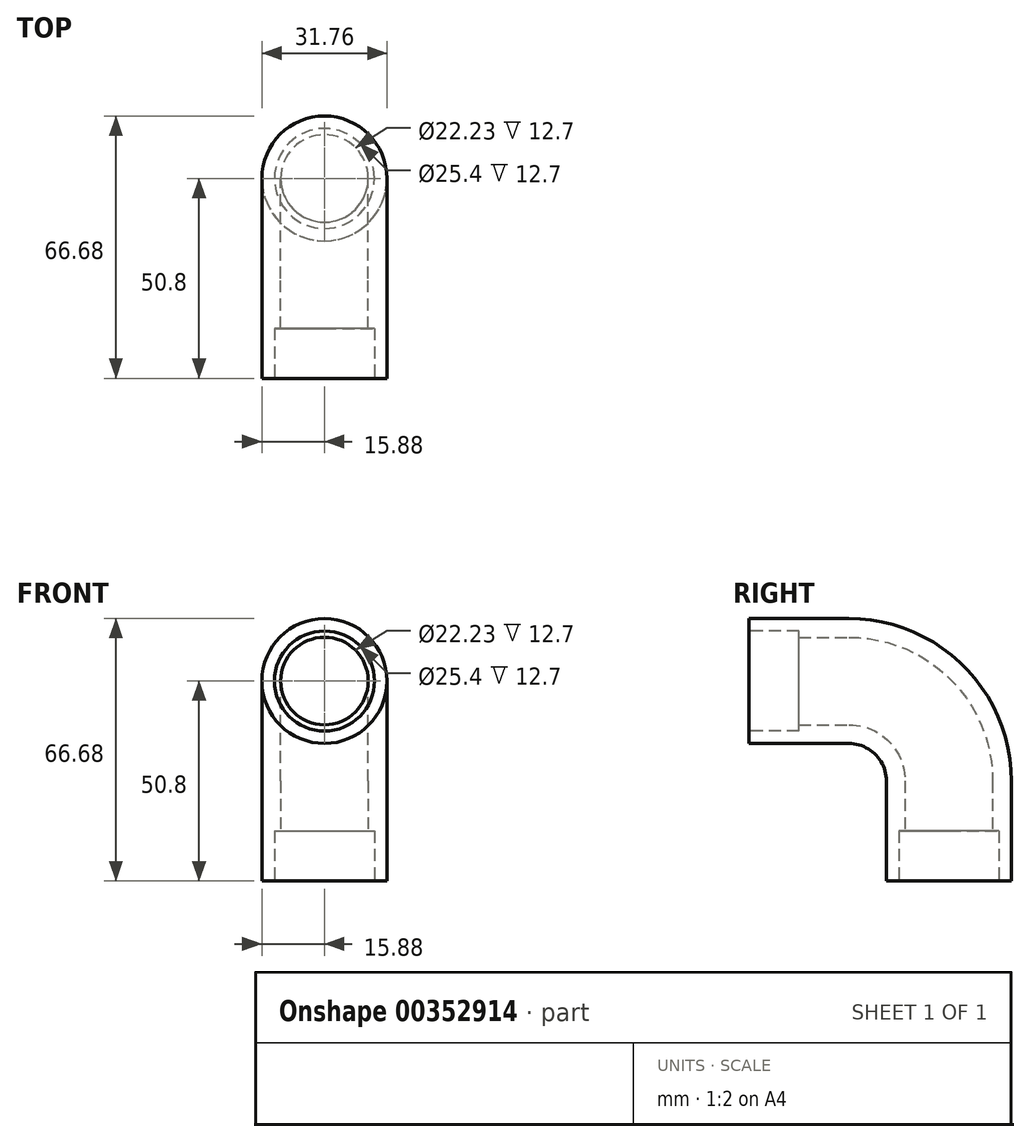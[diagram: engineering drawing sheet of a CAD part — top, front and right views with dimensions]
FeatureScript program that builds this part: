
annotation { "Feature Type Name" : "Feature", "Feature Type Description" : "" }
export const myFeature = defineFeature(function(context is Context, id is Id, definition is map)
    precondition{}
    {
        {
            var Q0;
            Q0=qCreatedBy(makeId("Front.planeOp"),FACE);
            var sketch = newSketch(context, id + "F0", { "sketchPlane" : qUnion([Q0])});
            skCircle(sketch, "E0", {"center": v(0, 0) * mm, "radius": 15.88 * mm});
            skCircle(sketch, "E1", {"center": v(0, 0) * mm, "radius": 11.11 * mm});
            skSolve(sketch);
        }
        {
            var Q0;
            Q0=qCreatedBy(makeId("Right.planeOp"),FACE);
            var sketch = newSketch(context, id + "F1", { "sketchPlane" : qUnion([Q0])});
            skLineSegment(sketch, "E2", {"start": v(0, 0) * mm, "end": v(25.4, 0) * mm});
            skLineSegment(sketch, "E3", {"start": v(50.8, -25.4) * mm, "end": v(50.8, -50.8) * mm});
            skPoint(sketch, "E4.visualSharp", {"position": v(50.8, 0) * mm});
            skArc(sketch, "E4.filletArc", {"start": v(50.8, -25.4) * mm, "mid": v(43.36, -7.44) * mm, "end": v(25.4, 0) * mm});
            skSolve(sketch);
        }
        {
            var Q0;
            Q0=makeQuery(id+"F0.imprint","IMPRINT",FACE,{"disambiguationData":[TD([[makeQuery(id+"F0.imprint","IMPRINT",EDGE,{"derivedFrom":sQuery(id+"F0.wireOp",EDGE,"E0")}),1.0]])]});
            var Q1;
            Q1=sQuery(id+"F1.wireOp",EDGE,"E2");
            var Q2;
            Q2=sQuery(id+"F1.wireOp",EDGE,"E4.filletArc");
            var Q3;
            Q3=sQuery(id+"F1.wireOp",EDGE,"E3");
            sweep(context, id + "F2", {"profiles" : qUnion([Q0]), "path" : qUnion([Q1, Q2, Q3])});
        }
        {
            var Q0;
            Q0=makeQuery(id+"F2.opSweep","CAP_FACE",FACE,{"disambiguationData":[OSD([sQuery(id+"F0.wireOp",EDGE,"E0"),sQuery(id+"F0.wireOp",EDGE,"E1"),sQuery(id+"F1.wireOp",VERTEX,"E2.start")])],"isStart":true});
            var sketch = newSketch(context, id + "F3", { "sketchPlane" : qUnion([Q0])});
            skCircle(sketch, "E5", {"center": v(0, 0) * mm, "radius": 12.7 * mm});
            skSolve(sketch);
        }
        {
            var Q0;
            Q0=qSketchRegion(id+"F3",true);
            extrude(context, id + "F4", {"entities" : qUnion([Q0]), "operationType" : NewBodyOperationType.REMOVE, "oppositeDirection" : true, "depth" : 12.7 * mm});
        }
        {
            var Q0;
            Q0=makeQuery(id+"F2.opSweep","CAP_FACE",FACE,{"disambiguationData":[OSD([sQuery(id+"F0.wireOp",EDGE,"E0"),sQuery(id+"F0.wireOp",EDGE,"E1"),sQuery(id+"F1.wireOp",VERTEX,"E3.end")])],"isStart":false});
            var sketch = newSketch(context, id + "F5", { "sketchPlane" : qUnion([Q0])});
            skCircle(sketch, "E6", {"center": v(0, -50.8) * mm, "radius": 12.7 * mm});
            skSolve(sketch);
        }
        {
            var Q0;
            Q0=qSketchRegion(id+"F5",true);
            extrude(context, id + "F6", {"entities" : qUnion([Q0]), "operationType" : NewBodyOperationType.REMOVE, "oppositeDirection" : true, "depth" : 12.7 * mm});
        }
    });
